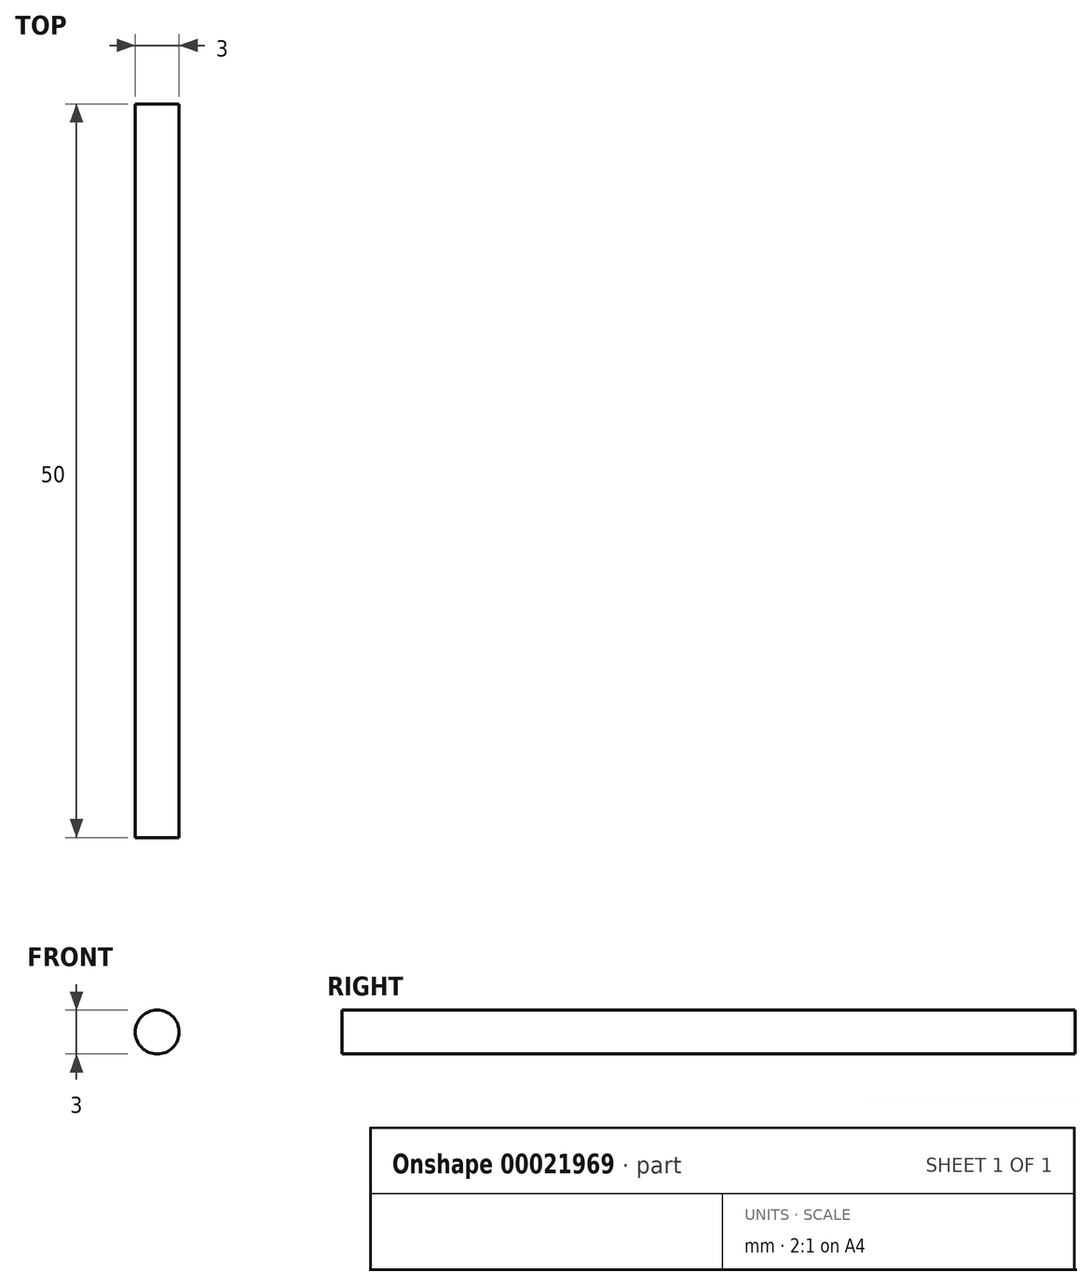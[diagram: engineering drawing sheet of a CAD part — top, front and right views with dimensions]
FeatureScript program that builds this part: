
annotation { "Feature Type Name" : "Feature", "Feature Type Description" : "" }
export const myFeature = defineFeature(function(context is Context, id is Id, definition is map)
    precondition{}
    {
        {
            var Q0;
            Q0=qCreatedBy(makeId("Front.planeOp"),FACE);
            var sketch = newSketch(context, id + "F0", { "sketchPlane" : qUnion([Q0])});
            skCircle(sketch, "E0", {"center": v(0, 0) * mm, "radius": 1.5 * mm});
            skSolve(sketch);
        }
        {
            var Q0;
            Q0=makeQuery(id+"F0.imprint","IMPRINT",FACE,{"disambiguationData":[TD([[makeQuery(id+"F0.imprint","IMPRINT",EDGE,{"derivedFrom":sQuery(id+"F0.wireOp",EDGE,"E0")}),1.0]])]});
            extrude(context, id + "F1", {"entities" : qUnion([Q0]), "endBound" : BoundingType.SYMMETRIC, "depth" : 50 * mm});
        }
    });
